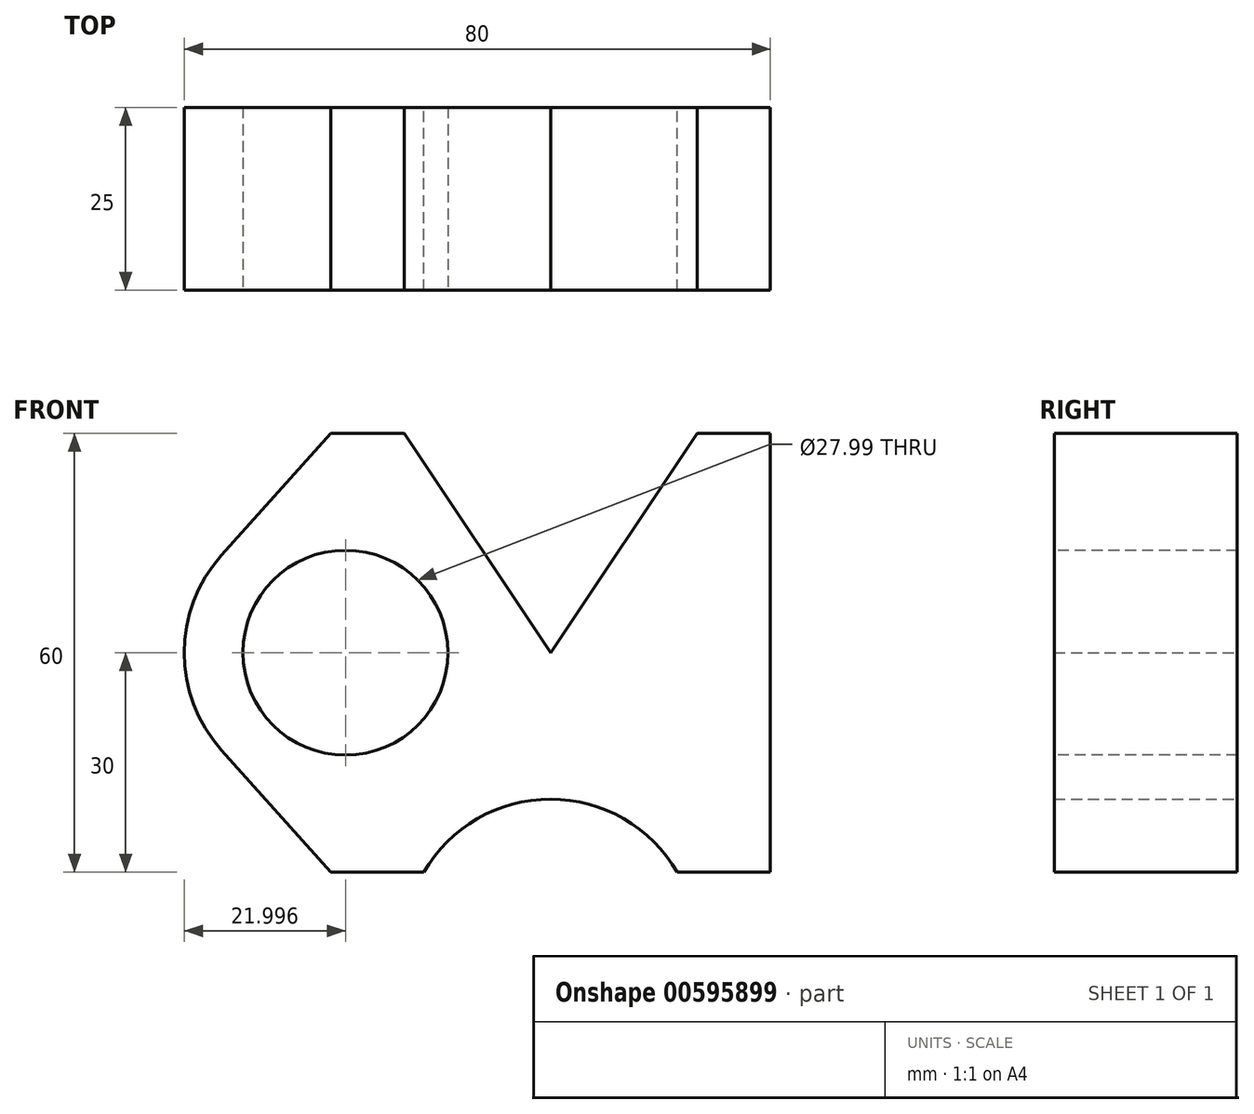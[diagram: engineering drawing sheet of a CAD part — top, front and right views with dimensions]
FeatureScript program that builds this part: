
annotation { "Feature Type Name" : "Feature", "Feature Type Description" : "" }
export const myFeature = defineFeature(function(context is Context, id is Id, definition is map)
    precondition{}
    {
        {
            var Q0;
            Q0=qCreatedBy(makeId("Front.planeOp"),FACE);
            var sketch = newSketch(context, id + "F0", { "sketchPlane" : qUnion([Q0])});
            skLineSegment(sketch, "E0", {"start": v(0, 0) * mm, "end": v(20, 30) * mm});
            skLineSegment(sketch, "E1", {"start": v(20, 30) * mm, "end": v(30, 30) * mm});
            skLineSegment(sketch, "E2", {"start": v(30, 30) * mm, "end": v(30, -30) * mm});
            skLineSegment(sketch, "E3", {"start": v(30, -30) * mm, "end": v(17.32, -30) * mm});
            skLineSegment(sketch, "E4", {"start": v(0, 0) * mm, "end": v(-20, 30) * mm});
            skLineSegment(sketch, "E5", {"start": v(-20, 30) * mm, "end": v(-30, 30) * mm});
            skLineSegment(sketch, "E6", {"start": v(-30, 30) * mm, "end": v(-44.9, 13.33) * mm});
            skArc(sketch, "E7", {"start": v(-44.9, 13.33) * mm, "mid": v(-50, 0) * mm, "end": v(-44.9, -13.33) * mm});
            skLineSegment(sketch, "E8", {"start": v(-44.9, -13.33) * mm, "end": v(-30, -30) * mm});
            skLineSegment(sketch, "E9", {"start": v(-30, -30) * mm, "end": v(-17.32, -30) * mm});
            skArc(sketch, "E10", {"start": v(17.32, -30) * mm, "mid": v(0, -20) * mm, "end": v(-17.32, -30) * mm});
            skLineSegment(sketch, "E11", {"start": v(-30, 30) * mm, "end": v(-30, -30) * mm, "construction": true});
            skSolve(sketch);
        }
        {
            var Q0;
            Q0=makeQuery(id+"F0.imprint","IMPRINT",FACE,{"disambiguationData":[TD([[makeQuery(id+"F0.imprint","IMPRINT",EDGE,{"derivedFrom":sQuery(id+"F0.wireOp",EDGE,"E0")}),-1.0]])]});
            extrude(context, id + "F1", {"entities" : qUnion([Q0]), "depth" : 25 * mm, "offsetDistance" : 25 * mm});
        }
        {
            var Q0;
            Q0=makeQuery(id+"F1.opExtrude","CAP_FACE",FACE,{"disambiguationData":[OSD([sQuery(id+"F0.wireOp",EDGE,"E0"),sQuery(id+"F0.wireOp",EDGE,"E1"),sQuery(id+"F0.wireOp",EDGE,"E2"),sQuery(id+"F0.wireOp",EDGE,"E3"),sQuery(id+"F0.wireOp",EDGE,"E4"),sQuery(id+"F0.wireOp",EDGE,"E5"),sQuery(id+"F0.wireOp",EDGE,"E6"),sQuery(id+"F0.wireOp",EDGE,"E7"),sQuery(id+"F0.wireOp",EDGE,"E8"),sQuery(id+"F0.wireOp",EDGE,"E9"),sQuery(id+"F0.wireOp",EDGE,"E10")])],"isStart":false});
            var sketch = newSketch(context, id + "F2", { "sketchPlane" : qUnion([Q0])});
            skCircle(sketch, "E12", {"center": v(-28, 0) * mm, "radius": 14 * mm});
            skSolve(sketch);
        }
        {
            var Q0;
            Q0=makeQuery(id+"F2.imprint","IMPRINT",FACE,{"disambiguationData":[TD([[makeQuery(id+"F2.imprint","IMPRINT",EDGE,{"derivedFrom":sQuery(id+"F2.wireOp",EDGE,"E12")}),1.0]])]});
            extrude(context, id + "F3", {"entities" : qUnion([Q0]), "operationType" : NewBodyOperationType.REMOVE, "endBound" : BoundingType.UP_TO_NEXT, "oppositeDirection" : true, "depth" : 25 * mm, "offsetDistance" : 25 * mm});
        }
    });
